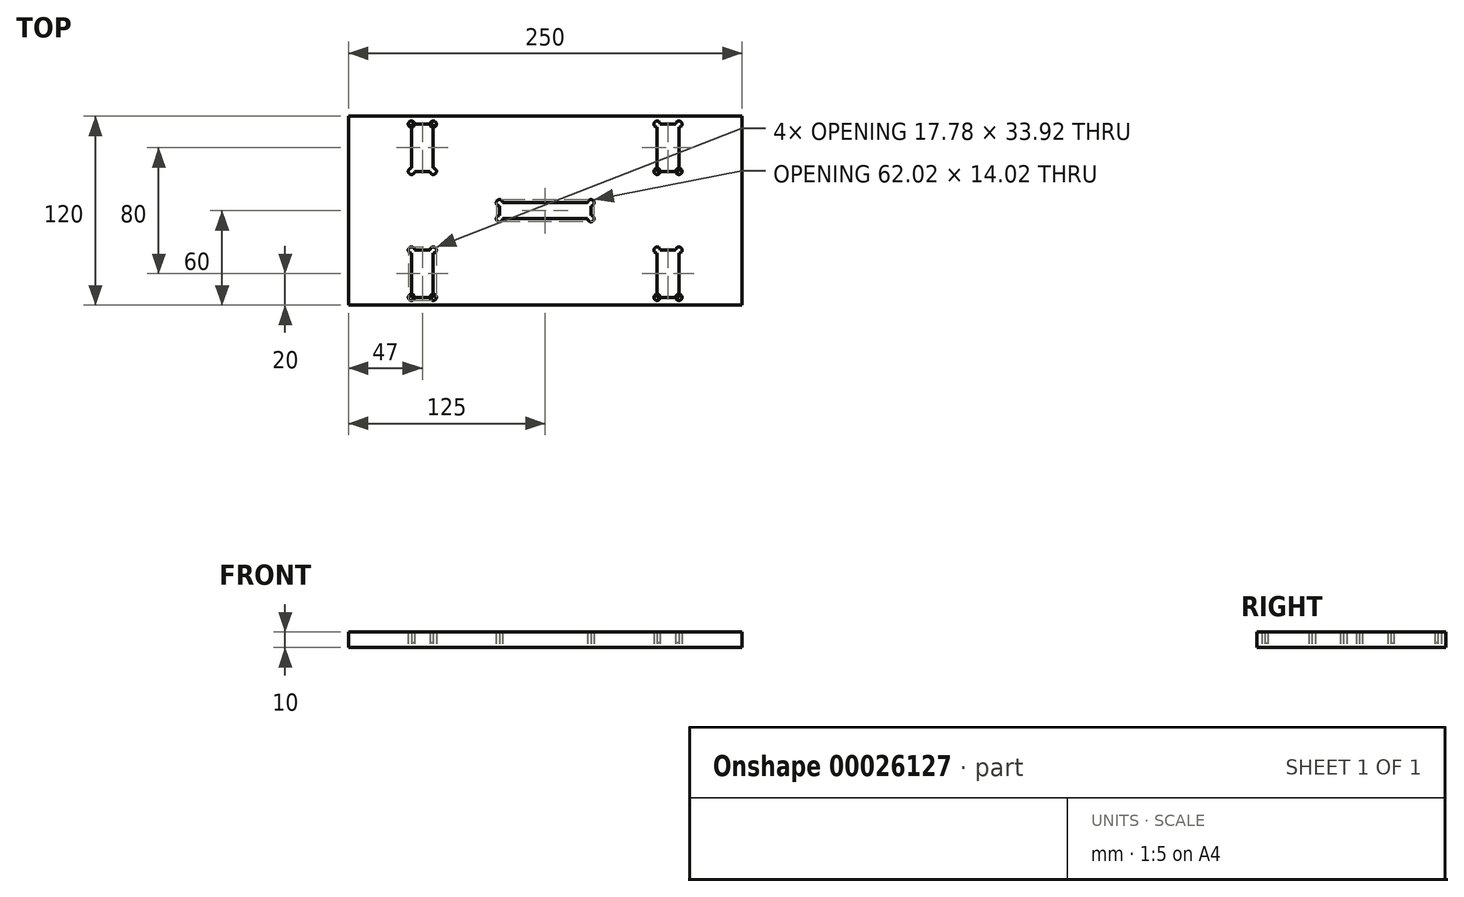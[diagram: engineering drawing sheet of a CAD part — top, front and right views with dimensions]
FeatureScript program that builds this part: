
annotation { "Feature Type Name" : "Feature", "Feature Type Description" : "" }
export const myFeature = defineFeature(function(context is Context, id is Id, definition is map)
    precondition{}
    {
        {
            var Q0;
            Q0=qCreatedBy(makeId("Top.planeOp"),FACE);
            var sketch = newSketch(context, id + "F0", { "sketchPlane" : qUnion([Q0])});
            skLineSegment(sketch, "E0.rect.bottom", {"start": v(125, -60) * mm, "end": v(-125, -60) * mm});
            skLineSegment(sketch, "E0.rect.top", {"start": v(125, 60) * mm, "end": v(-125, 60) * mm});
            skLineSegment(sketch, "E0.rect.left", {"start": v(125, -60) * mm, "end": v(125, 60) * mm});
            skLineSegment(sketch, "E0.rect.right", {"start": v(-125, -60) * mm, "end": v(-125, 60) * mm});
            skPoint(sketch, "E0.rect.middle", {"position": v(0, 0) * mm});
            skLineSegment(sketch, "E1", {"start": v(-78, 60) * mm, "end": v(-78, -60) * mm, "construction": true});
            skLineSegment(sketch, "E2", {"start": v(-78, -60) * mm, "end": v(78, 60) * mm, "construction": true});
            skLineSegment(sketch, "E3", {"start": v(78, 60) * mm, "end": v(78, -60) * mm, "construction": true});
            skLineSegment(sketch, "E4", {"start": v(-125, 55) * mm, "end": v(125, 55) * mm, "construction": true});
            skLineSegment(sketch, "E5", {"start": v(-125, -55) * mm, "end": v(125, -55) * mm, "construction": true});
            skLineSegment(sketch, "E6.rect.bottom", {"start": v(-71.07, 55) * mm, "end": v(-84.93, 55) * mm});
            skLineSegment(sketch, "E6.rect.top", {"start": v(-71.07, 25) * mm, "end": v(-84.93, 25) * mm});
            skLineSegment(sketch, "E6.rect.left", {"start": v(-71.07, 55) * mm, "end": v(-71.07, 25) * mm});
            skLineSegment(sketch, "E6.rect.right", {"start": v(-84.93, 55) * mm, "end": v(-84.93, 25) * mm});
            skPoint(sketch, "E6.rect.middle", {"position": v(-78, 40) * mm});
            skLineSegment(sketch, "E7.rect.bottom", {"start": v(-71.07, -55) * mm, "end": v(-84.93, -55) * mm});
            skLineSegment(sketch, "E7.rect.top", {"start": v(-71.07, -25) * mm, "end": v(-84.93, -25) * mm});
            skLineSegment(sketch, "E7.rect.left", {"start": v(-71.07, -55) * mm, "end": v(-71.07, -25) * mm});
            skLineSegment(sketch, "E7.rect.right", {"start": v(-84.93, -55) * mm, "end": v(-84.93, -25) * mm});
            skPoint(sketch, "E7.rect.middle", {"position": v(-78, -40) * mm});
            skLineSegment(sketch, "E8.rect.bottom", {"start": v(84.93, 25) * mm, "end": v(71.07, 25) * mm});
            skLineSegment(sketch, "E8.rect.top", {"start": v(84.93, 55) * mm, "end": v(71.07, 55) * mm});
            skLineSegment(sketch, "E8.rect.left", {"start": v(84.93, 25) * mm, "end": v(84.93, 55) * mm});
            skLineSegment(sketch, "E8.rect.right", {"start": v(71.07, 25) * mm, "end": v(71.07, 55) * mm});
            skPoint(sketch, "E8.rect.middle", {"position": v(78, 40) * mm});
            skLineSegment(sketch, "E9.rect.bottom", {"start": v(84.93, -55) * mm, "end": v(71.07, -55) * mm});
            skLineSegment(sketch, "E9.rect.top", {"start": v(84.93, -25) * mm, "end": v(71.07, -25) * mm});
            skLineSegment(sketch, "E9.rect.left", {"start": v(84.93, -55) * mm, "end": v(84.93, -25) * mm});
            skLineSegment(sketch, "E9.rect.right", {"start": v(71.07, -55) * mm, "end": v(71.07, -25) * mm});
            skPoint(sketch, "E9.rect.middle", {"position": v(78, -40) * mm});
            skCircle(sketch, "E10", {"center": v(-201.5, 0) * mm, "radius": 9.5 * mm, "construction": true});
            skLineSegment(sketch, "E11", {"start": v(-227.26, 9.5) * mm, "end": v(-166.14, 9.5) * mm, "construction": true});
            skLineSegment(sketch, "E12", {"start": v(-166.14, 6.5) * mm, "end": v(-227.26, 6.5) * mm, "construction": true});
            skLineSegment(sketch, "E13", {"start": v(-208.44, 9.5) * mm, "end": v(-208.44, 6.5) * mm});
            skLineSegment(sketch, "E14", {"start": v(-194.58, 9.5) * mm, "end": v(-194.58, 6.5) * mm});
            skLineSegment(sketch, "E15.rect.bottom", {"start": v(27.05, 5.05) * mm, "end": v(-27.05, 5.05) * mm});
            skLineSegment(sketch, "E15.rect.top", {"start": v(27.05, -5.05) * mm, "end": v(-27.05, -5.05) * mm});
            skLineSegment(sketch, "E15.rect.left", {"start": v(29.05, 3.05) * mm, "end": v(29.05, -3.05) * mm});
            skLineSegment(sketch, "E15.rect.right", {"start": v(-29.05, 3.05) * mm, "end": v(-29.05, -3.05) * mm});
            skLineSegment(sketch, "E16.rect.bottom", {"start": v(87.5, -55) * mm, "end": v(68.5, -55) * mm, "construction": true});
            skLineSegment(sketch, "E16.rect.top", {"start": v(87.5, -25) * mm, "end": v(68.5, -25) * mm, "construction": true});
            skLineSegment(sketch, "E16.rect.left", {"start": v(87.5, -55) * mm, "end": v(87.5, -42.5) * mm, "construction": true});
            skLineSegment(sketch, "E16.rect.right", {"start": v(68.5, -55) * mm, "end": v(68.5, -42.5) * mm, "construction": true});
            skLineSegment(sketch, "E17.rect.bottom", {"start": v(88.5, -37.5) * mm, "end": v(89.5, -37.5) * mm, "construction": true});
            skLineSegment(sketch, "E17.rect.top", {"start": v(88.5, -42.5) * mm, "end": v(89.5, -42.5) * mm, "construction": true});
            skLineSegment(sketch, "E17.rect.left", {"start": v(87.5, -39.5) * mm, "end": v(87.5, -42.5) * mm, "construction": true});
            skLineSegment(sketch, "E17.rect.right", {"start": v(90.5, -39.5) * mm, "end": v(90.5, -40.5) * mm, "construction": true});
            skPoint(sketch, "E17.rect.middle", {"position": v(89, -40) * mm});
            skLineSegment(sketch, "E18.rect.bottom", {"start": v(67.5, -37.5) * mm, "end": v(66.5, -37.5) * mm, "construction": true});
            skLineSegment(sketch, "E18.rect.top", {"start": v(67.5, -42.5) * mm, "end": v(66.5, -42.5) * mm, "construction": true});
            skLineSegment(sketch, "E18.rect.left", {"start": v(68.5, -39.5) * mm, "end": v(68.5, -42.5) * mm, "construction": true});
            skLineSegment(sketch, "E18.rect.right", {"start": v(65.5, -39.5) * mm, "end": v(65.5, -40.5) * mm, "construction": true});
            skPoint(sketch, "E18.rect.middle", {"position": v(67, -40) * mm});
            skLineSegment(sketch, "E19", {"start": v(0, -60) * mm, "end": v(0, 0) * mm, "construction": true});
            skLineSegment(sketch, "E20", {"start": v(0, 0) * mm, "end": v(125, 0) * mm, "construction": true});
            skLineSegment(sketch, "E21.MirrorCS", {"start": v(87.5, 39.5) * mm, "end": v(87.5, 40.5) * mm, "construction": true});
            skLineSegment(sketch, "E22.MirrorCS", {"start": v(88.5, 42.5) * mm, "end": v(89.5, 42.5) * mm, "construction": true});
            skLineSegment(sketch, "E23.MirrorCS", {"start": v(90.5, 39.5) * mm, "end": v(90.5, 40.5) * mm, "construction": true});
            skLineSegment(sketch, "E24.MirrorCS", {"start": v(88.5, 37.5) * mm, "end": v(89.5, 37.5) * mm, "construction": true});
            skLineSegment(sketch, "E25.MirrorCS", {"start": v(68.5, 39.5) * mm, "end": v(68.5, 40.5) * mm, "construction": true});
            skLineSegment(sketch, "E26.MirrorCS", {"start": v(67.5, 42.5) * mm, "end": v(66.5, 42.5) * mm, "construction": true});
            skLineSegment(sketch, "E27.MirrorCS", {"start": v(65.5, 39.5) * mm, "end": v(65.5, 40.5) * mm, "construction": true});
            skLineSegment(sketch, "E28.MirrorCS", {"start": v(67.5, 37.5) * mm, "end": v(66.5, 37.5) * mm, "construction": true});
            skLineSegment(sketch, "E29.MirrorCS", {"start": v(-87.5, -39.5) * mm, "end": v(-87.5, -40.5) * mm, "construction": true});
            skLineSegment(sketch, "E30.MirrorCS", {"start": v(-88.5, -42.5) * mm, "end": v(-89.5, -42.5) * mm, "construction": true});
            skLineSegment(sketch, "E31.MirrorCS", {"start": v(-90.5, -39.5) * mm, "end": v(-90.5, -40.5) * mm, "construction": true});
            skLineSegment(sketch, "E32.MirrorCS", {"start": v(-88.5, -37.5) * mm, "end": v(-89.5, -37.5) * mm, "construction": true});
            skLineSegment(sketch, "E33.MirrorCS", {"start": v(-67.5, -37.5) * mm, "end": v(-66.5, -37.5) * mm, "construction": true});
            skLineSegment(sketch, "E34.MirrorCS", {"start": v(-68.5, -39.5) * mm, "end": v(-68.5, -40.5) * mm, "construction": true});
            skLineSegment(sketch, "E35.MirrorCS", {"start": v(-67.5, -42.5) * mm, "end": v(-66.5, -42.5) * mm, "construction": true});
            skLineSegment(sketch, "E36.MirrorCS", {"start": v(-65.5, -39.5) * mm, "end": v(-65.5, -40.5) * mm, "construction": true});
            skLineSegment(sketch, "E37.MirrorCS", {"start": v(-87.5, 39.5) * mm, "end": v(-87.5, 40.5) * mm, "construction": true});
            skLineSegment(sketch, "E38.MirrorCS", {"start": v(-88.5, 37.5) * mm, "end": v(-89.5, 37.5) * mm, "construction": true});
            skLineSegment(sketch, "E39.MirrorCS", {"start": v(-90.5, 39.5) * mm, "end": v(-90.5, 40.5) * mm, "construction": true});
            skLineSegment(sketch, "E40.MirrorCS", {"start": v(-88.5, 42.5) * mm, "end": v(-89.5, 42.5) * mm, "construction": true});
            skLineSegment(sketch, "E41.MirrorCS", {"start": v(-67.5, 42.5) * mm, "end": v(-66.5, 42.5) * mm, "construction": true});
            skLineSegment(sketch, "E42.MirrorCS", {"start": v(-68.5, 39.5) * mm, "end": v(-68.5, 40.5) * mm, "construction": true});
            skLineSegment(sketch, "E43.MirrorCS", {"start": v(-67.5, 37.5) * mm, "end": v(-66.5, 37.5) * mm, "construction": true});
            skLineSegment(sketch, "E44.MirrorCS", {"start": v(-65.5, 39.5) * mm, "end": v(-65.5, 40.5) * mm, "construction": true});
            skArc(sketch, "E45", {"start": v(-27.05, 5.05) * mm, "mid": v(-30.46, 6.46) * mm, "end": v(-29.05, 3.05) * mm});
            skArc(sketch, "E46", {"start": v(-29.05, -3.05) * mm, "mid": v(-30.46, -6.46) * mm, "end": v(-27.05, -5.05) * mm});
            skArc(sketch, "E47", {"start": v(29.05, 3.05) * mm, "mid": v(30.46, 6.46) * mm, "end": v(27.05, 5.05) * mm});
            skArc(sketch, "E48", {"start": v(27.05, -5.05) * mm, "mid": v(30.46, -6.46) * mm, "end": v(29.05, -3.05) * mm});
            skArc(sketch, "E49", {"start": v(67.5, 42.5) * mm, "mid": v(64.09, 43.91) * mm, "end": v(65.5, 40.5) * mm, "construction": true});
            skArc(sketch, "E50", {"start": v(65.5, 39.5) * mm, "mid": v(64.09, 36.09) * mm, "end": v(67.5, 37.5) * mm, "construction": true});
            skArc(sketch, "E51", {"start": v(66.5, 37.5) * mm, "mid": v(69.91, 36.09) * mm, "end": v(68.5, 39.5) * mm, "construction": true});
            skArc(sketch, "E52", {"start": v(68.5, 40.5) * mm, "mid": v(69.91, 43.91) * mm, "end": v(66.5, 42.5) * mm, "construction": true});
            skArc(sketch, "E53", {"start": v(89.5, 42.5) * mm, "mid": v(86.09, 43.91) * mm, "end": v(87.5, 40.5) * mm, "construction": true});
            skArc(sketch, "E54", {"start": v(90.5, 40.5) * mm, "mid": v(91.91, 43.91) * mm, "end": v(88.5, 42.5) * mm, "construction": true});
            skArc(sketch, "E55", {"start": v(88.5, 37.5) * mm, "mid": v(91.91, 36.09) * mm, "end": v(90.5, 39.5) * mm, "construction": true});
            skArc(sketch, "E56", {"start": v(87.5, 39.5) * mm, "mid": v(86.09, 36.09) * mm, "end": v(89.5, 37.5) * mm, "construction": true});
            skArc(sketch, "E57", {"start": v(67.5, -37.5) * mm, "mid": v(64.09, -36.09) * mm, "end": v(65.5, -39.5) * mm, "construction": true});
            skArc(sketch, "E58", {"start": v(68.5, -39.5) * mm, "mid": v(69.91, -36.09) * mm, "end": v(66.5, -37.5) * mm, "construction": true});
            skArc(sketch, "E59", {"start": v(65.5, -40.5) * mm, "mid": v(64.09, -43.91) * mm, "end": v(67.5, -42.5) * mm, "construction": true});
            skArc(sketch, "E60", {"start": v(66.5, -42.5) * mm, "mid": v(69.91, -43.91) * mm, "end": v(68.5, -40.5) * mm, "construction": true});
            skArc(sketch, "E61", {"start": v(89.5, -37.5) * mm, "mid": v(86.09, -36.09) * mm, "end": v(87.5, -39.5) * mm, "construction": true});
            skArc(sketch, "E62", {"start": v(90.5, -39.5) * mm, "mid": v(91.91, -36.09) * mm, "end": v(88.5, -37.5) * mm, "construction": true});
            skArc(sketch, "E63", {"start": v(88.5, -42.5) * mm, "mid": v(91.91, -43.91) * mm, "end": v(90.5, -40.5) * mm, "construction": true});
            skArc(sketch, "E64", {"start": v(87.5, -40.5) * mm, "mid": v(86.09, -43.91) * mm, "end": v(89.5, -42.5) * mm, "construction": true});
            skArc(sketch, "E65", {"start": v(-88.5, 42.5) * mm, "mid": v(-91.91, 43.91) * mm, "end": v(-90.5, 40.5) * mm, "construction": true});
            skArc(sketch, "E66", {"start": v(-87.5, 40.5) * mm, "mid": v(-86.09, 43.91) * mm, "end": v(-89.5, 42.5) * mm, "construction": true});
            skArc(sketch, "E67", {"start": v(-90.5, 39.5) * mm, "mid": v(-91.91, 36.09) * mm, "end": v(-88.5, 37.5) * mm, "construction": true});
            skArc(sketch, "E68", {"start": v(-89.5, 37.5) * mm, "mid": v(-86.09, 36.09) * mm, "end": v(-87.5, 39.5) * mm, "construction": true});
            skArc(sketch, "E69", {"start": v(-66.5, 42.5) * mm, "mid": v(-69.91, 43.91) * mm, "end": v(-68.5, 40.5) * mm, "construction": true});
            skArc(sketch, "E70", {"start": v(-65.5, 40.5) * mm, "mid": v(-64.09, 43.91) * mm, "end": v(-67.5, 42.5) * mm, "construction": true});
            skArc(sketch, "E71", {"start": v(-68.5, 39.5) * mm, "mid": v(-69.91, 36.09) * mm, "end": v(-66.5, 37.5) * mm, "construction": true});
            skArc(sketch, "E72", {"start": v(-67.5, 37.5) * mm, "mid": v(-64.09, 36.09) * mm, "end": v(-65.5, 39.5) * mm, "construction": true});
            skArc(sketch, "E73", {"start": v(-88.5, -37.5) * mm, "mid": v(-91.91, -36.09) * mm, "end": v(-90.5, -39.5) * mm, "construction": true});
            skArc(sketch, "E74", {"start": v(-87.5, -39.5) * mm, "mid": v(-86.09, -36.09) * mm, "end": v(-89.5, -37.5) * mm, "construction": true});
            skArc(sketch, "E75", {"start": v(-90.5, -40.5) * mm, "mid": v(-91.91, -43.91) * mm, "end": v(-88.5, -42.5) * mm, "construction": true});
            skArc(sketch, "E76", {"start": v(-89.5, -42.5) * mm, "mid": v(-86.09, -43.91) * mm, "end": v(-87.5, -40.5) * mm, "construction": true});
            skArc(sketch, "E77", {"start": v(-66.5, -37.5) * mm, "mid": v(-69.91, -36.09) * mm, "end": v(-68.5, -39.5) * mm, "construction": true});
            skArc(sketch, "E78", {"start": v(-65.5, -39.5) * mm, "mid": v(-64.09, -36.09) * mm, "end": v(-67.5, -37.5) * mm, "construction": true});
            skArc(sketch, "E79", {"start": v(-68.5, -40.5) * mm, "mid": v(-69.91, -43.91) * mm, "end": v(-66.5, -42.5) * mm, "construction": true});
            skArc(sketch, "E80", {"start": v(-67.5, -42.5) * mm, "mid": v(-64.09, -43.91) * mm, "end": v(-65.5, -40.5) * mm, "construction": true});
            skLineSegment(sketch, "E81.trimOffspring", {"start": v(68.5, -40.5) * mm, "end": v(68.5, -25) * mm, "construction": true});
            skLineSegment(sketch, "E82.trimOffspring", {"start": v(87.5, -40.5) * mm, "end": v(87.5, -25) * mm, "construction": true});
            skLineSegment(sketch, "E83.bottom", {"start": v(-90.5, -42.5) * mm, "end": v(-87.5, -42.5) * mm, "construction": true});
            skLineSegment(sketch, "E83.top", {"start": v(-90.5, -37.5) * mm, "end": v(-87.5, -37.5) * mm, "construction": true});
            skLineSegment(sketch, "E83.left", {"start": v(-90.5, -42.5) * mm, "end": v(-90.5, -37.5) * mm, "construction": true});
            skLineSegment(sketch, "E83.right", {"start": v(-87.5, -42.5) * mm, "end": v(-87.5, -37.5) * mm, "construction": true});
            skLineSegment(sketch, "E84.bottom", {"start": v(-68.5, 42.5) * mm, "end": v(-65.5, 42.5) * mm, "construction": true});
            skLineSegment(sketch, "E84.top", {"start": v(-68.5, 37.5) * mm, "end": v(-65.5, 37.5) * mm, "construction": true});
            skLineSegment(sketch, "E84.left", {"start": v(-68.5, 42.5) * mm, "end": v(-68.5, 37.5) * mm, "construction": true});
            skLineSegment(sketch, "E84.right", {"start": v(-65.5, 42.5) * mm, "end": v(-65.5, 37.5) * mm, "construction": true});
            skLineSegment(sketch, "E85.bottom", {"start": v(-90.5, 42.5) * mm, "end": v(-87.5, 42.5) * mm, "construction": true});
            skLineSegment(sketch, "E85.top", {"start": v(-90.5, 37.5) * mm, "end": v(-87.5, 37.5) * mm, "construction": true});
            skLineSegment(sketch, "E85.left", {"start": v(-90.5, 42.5) * mm, "end": v(-90.5, 37.5) * mm, "construction": true});
            skLineSegment(sketch, "E85.right", {"start": v(-87.5, 42.5) * mm, "end": v(-87.5, 37.5) * mm, "construction": true});
            skLineSegment(sketch, "E86.bottom", {"start": v(-68.5, -37.5) * mm, "end": v(-65.5, -37.5) * mm, "construction": true});
            skLineSegment(sketch, "E86.top", {"start": v(-68.5, -42.5) * mm, "end": v(-65.5, -42.5) * mm, "construction": true});
            skLineSegment(sketch, "E86.left", {"start": v(-68.5, -37.5) * mm, "end": v(-68.5, -42.5) * mm, "construction": true});
            skLineSegment(sketch, "E86.right", {"start": v(-65.5, -37.5) * mm, "end": v(-65.5, -42.5) * mm, "construction": true});
            skLineSegment(sketch, "E87.bottom", {"start": v(65.5, -37.5) * mm, "end": v(68.5, -37.5) * mm, "construction": true});
            skLineSegment(sketch, "E87.top", {"start": v(65.5, -42.5) * mm, "end": v(68.5, -42.5) * mm, "construction": true});
            skLineSegment(sketch, "E87.left", {"start": v(65.5, -37.5) * mm, "end": v(65.5, -42.5) * mm, "construction": true});
            skLineSegment(sketch, "E87.right", {"start": v(68.5, -37.5) * mm, "end": v(68.5, -42.5) * mm, "construction": true});
            skLineSegment(sketch, "E88.bottom", {"start": v(87.5, -37.5) * mm, "end": v(90.5, -37.5) * mm, "construction": true});
            skLineSegment(sketch, "E88.top", {"start": v(87.5, -42.5) * mm, "end": v(90.5, -42.5) * mm, "construction": true});
            skLineSegment(sketch, "E88.left", {"start": v(87.5, -37.5) * mm, "end": v(87.5, -42.5) * mm, "construction": true});
            skLineSegment(sketch, "E88.right", {"start": v(90.5, -37.5) * mm, "end": v(90.5, -42.5) * mm, "construction": true});
            skLineSegment(sketch, "E89.bottom", {"start": v(87.5, 42.5) * mm, "end": v(90.5, 42.5) * mm, "construction": true});
            skLineSegment(sketch, "E89.top", {"start": v(87.5, 37.5) * mm, "end": v(90.5, 37.5) * mm, "construction": true});
            skLineSegment(sketch, "E89.left", {"start": v(87.5, 42.5) * mm, "end": v(87.5, 37.5) * mm, "construction": true});
            skLineSegment(sketch, "E89.right", {"start": v(90.5, 42.5) * mm, "end": v(90.5, 37.5) * mm, "construction": true});
            skLineSegment(sketch, "E90.bottom", {"start": v(65.5, 42.5) * mm, "end": v(68.5, 42.5) * mm, "construction": true});
            skLineSegment(sketch, "E90.top", {"start": v(65.5, 37.5) * mm, "end": v(68.5, 37.5) * mm, "construction": true});
            skLineSegment(sketch, "E90.left", {"start": v(65.5, 42.5) * mm, "end": v(65.5, 37.5) * mm, "construction": true});
            skLineSegment(sketch, "E90.right", {"start": v(68.5, 42.5) * mm, "end": v(68.5, 37.5) * mm, "construction": true});
            skCircle(sketch, "E91", {"center": v(-84.93, 55) * mm, "radius": 2 * mm});
            skCircle(sketch, "E92", {"center": v(-71.07, 55) * mm, "radius": 2 * mm});
            skCircle(sketch, "E93", {"center": v(-84.93, 25) * mm, "radius": 2 * mm});
            skCircle(sketch, "E94", {"center": v(-71.07, 25) * mm, "radius": 2 * mm});
            skCircle(sketch, "E95.MirrorC", {"center": v(84.93, 55) * mm, "radius": 2 * mm});
            skCircle(sketch, "E96.MirrorC", {"center": v(71.07, 55) * mm, "radius": 2 * mm});
            skCircle(sketch, "E97.MirrorC", {"center": v(71.07, 25) * mm, "radius": 2 * mm});
            skCircle(sketch, "E98.MirrorC", {"center": v(84.93, 25) * mm, "radius": 2 * mm});
            skCircle(sketch, "E99.MirrorC", {"center": v(-71.07, -25) * mm, "radius": 2 * mm});
            skCircle(sketch, "E100.MirrorC", {"center": v(-84.93, -25) * mm, "radius": 2 * mm});
            skCircle(sketch, "E101.MirrorC", {"center": v(-84.93, -55) * mm, "radius": 2 * mm});
            skCircle(sketch, "E102.MirrorC", {"center": v(-71.07, -55) * mm, "radius": 2 * mm});
            skCircle(sketch, "E103.MirrorC", {"center": v(71.07, -55) * mm, "radius": 2 * mm});
            skCircle(sketch, "E104.MirrorC", {"center": v(84.93, -25) * mm, "radius": 2 * mm});
            skCircle(sketch, "E105.MirrorC", {"center": v(71.07, -25) * mm, "radius": 2 * mm});
            skCircle(sketch, "E106.MirrorC", {"center": v(84.93, -55) * mm, "radius": 2 * mm});
            skCircle(sketch, "E107", {"center": v(-29.05, 5.05) * mm, "radius": 2 * mm});
            skCircle(sketch, "E108", {"center": v(-29.05, -5.05) * mm, "radius": 2 * mm});
            skCircle(sketch, "E109", {"center": v(29.05, -5.05) * mm, "radius": 2 * mm});
            skCircle(sketch, "E110", {"center": v(29.05, 5.05) * mm, "radius": 2 * mm});
            skSolve(sketch);
        }
        {
            var Q0;
            Q0=makeQuery(id+"F0.imprint","IMPRINT",FACE,{"disambiguationData":[TD([[makeQuery(id+"F0.imprint","IMPRINT",EDGE,{"derivedFrom":sQuery(id+"F0.wireOp",EDGE,"E0.rect.bottom")}),-1.0]])]});
            var Q1;
            Q1=makeQuery(id+"F0.imprint","IMPRINT",FACE,{"disambiguationData":[TD([[makeQuery(id+"F0.imprint","IMPRINT",EDGE,{"derivedFrom":sQuery(id+"F0.wireOp",EDGE,"E6.rect.bottom")}),1.0]])]});
            var Q2;
            Q2=makeQuery(id+"F0.imprint","IMPRINT",FACE,{"disambiguationData":[TD([[makeQuery(id+"F0.imprint","IMPRINT",EDGE,{"derivedFrom":sQuery(id+"F0.wireOp",EDGE,"E7.rect.bottom")}),-1.0]])]});
            var Q3;
            Q3=makeQuery(id+"F0.imprint","IMPRINT",FACE,{"disambiguationData":[TD([[makeQuery(id+"F0.imprint","IMPRINT",EDGE,{"derivedFrom":sQuery(id+"F0.wireOp",EDGE,"E8.rect.bottom")}),-1.0]])]});
            var Q4;
            Q4=makeQuery(id+"F0.imprint","IMPRINT",FACE,{"disambiguationData":[TD([[makeQuery(id+"F0.imprint","IMPRINT",EDGE,{"derivedFrom":sQuery(id+"F0.wireOp",EDGE,"E9.rect.bottom")}),-1.0]])]});
            var Q5;
            Q5=makeQuery(id+"F0.imprint","IMPRINT",FACE,{"disambiguationData":[TD([[makeQuery(id+"F0.imprint","IMPRINT",EDGE,{"derivedFrom":sQuery(id+"F0.wireOp",EDGE,"E37.MirrorCS")}),1.0]])]});
            var Q6;
            Q6=makeQuery(id+"F0.imprint","IMPRINT",FACE,{"disambiguationData":[TD([[makeQuery(id+"F0.imprint","IMPRINT",EDGE,{"derivedFrom":sQuery(id+"F0.wireOp",EDGE,"E41.MirrorCS")}),-1.0]])]});
            var Q7;
            Q7=makeQuery(id+"F0.imprint","IMPRINT",FACE,{"disambiguationData":[TD([[makeQuery(id+"F0.imprint","IMPRINT",EDGE,{"derivedFrom":sQuery(id+"F0.wireOp",EDGE,"E29.MirrorCS")}),-1.0]])]});
            var Q8;
            Q8=makeQuery(id+"F0.imprint","IMPRINT",FACE,{"disambiguationData":[TD([[makeQuery(id+"F0.imprint","IMPRINT",EDGE,{"derivedFrom":sQuery(id+"F0.wireOp",EDGE,"E33.MirrorCS")}),-1.0]])]});
            var Q9;
            Q9=makeQuery(id+"F0.imprint","IMPRINT",FACE,{"disambiguationData":[TD([[makeQuery(id+"F0.imprint","IMPRINT",EDGE,{"derivedFrom":sQuery(id+"F0.wireOp",EDGE,"E25.MirrorCS")}),1.0]])]});
            var Q10;
            Q10=makeQuery(id+"F0.imprint","IMPRINT",FACE,{"disambiguationData":[TD([[makeQuery(id+"F0.imprint","IMPRINT",EDGE,{"derivedFrom":sQuery(id+"F0.wireOp",EDGE,"E21.MirrorCS")}),-1.0]])]});
            var Q11;
            Q11=makeQuery(id+"F0.imprint","IMPRINT",FACE,{"disambiguationData":[TD([[makeQuery(id+"F0.imprint","IMPRINT",EDGE,{"derivedFrom":sQuery(id+"F0.wireOp",EDGE,"E17.rect.bottom")}),-1.0]])]});
            var Q12;
            Q12=makeQuery(id+"F0.imprint","IMPRINT",FACE,{"disambiguationData":[TD([[makeQuery(id+"F0.imprint","IMPRINT",EDGE,{"derivedFrom":sQuery(id+"F0.wireOp",EDGE,"E18.rect.bottom")}),1.0]])]});
            extrude(context, id + "F1", {"entities" : qUnion([Q0, Q1, Q2, Q3, Q4, Q5, Q6, Q7, Q8, Q9, Q10, Q11, Q12]), "depth" : 10 * mm});
        }
        {
            var Q0;
            Q0=makeQuery(id+"F0.imprint","IMPRINT",FACE,{"disambiguationData":[TD([[makeQuery(id+"F0.imprint","IMPRINT",EDGE,{"derivedFrom":sQuery(id+"F0.wireOp",EDGE,"E8.rect.bottom")}),-1.0]])]});
            var Q1;
            Q1=makeQuery(id+"F0.imprint","IMPRINT",FACE,{"disambiguationData":[TD([[makeQuery(id+"F0.imprint","IMPRINT",EDGE,{"derivedFrom":sQuery(id+"F0.wireOp",EDGE,"E9.rect.bottom")}),-1.0]])]});
            var Q2;
            Q2=makeQuery(id+"F0.imprint","IMPRINT",FACE,{"disambiguationData":[TD([[makeQuery(id+"F0.imprint","IMPRINT",EDGE,{"derivedFrom":sQuery(id+"F0.wireOp",EDGE,"E6.rect.bottom")}),1.0]])]});
            var Q3;
            Q3=makeQuery(id+"F0.imprint","IMPRINT",FACE,{"disambiguationData":[TD([[makeQuery(id+"F0.imprint","IMPRINT",EDGE,{"derivedFrom":sQuery(id+"F0.wireOp",EDGE,"E7.rect.bottom")}),-1.0]])]});
            extrude(context, id + "F2", {"entities" : qUnion([Q0, Q1, Q2, Q3]), "operationType" : NewBodyOperationType.REMOVE, "depth" : 3 * mm});
        }
    });
